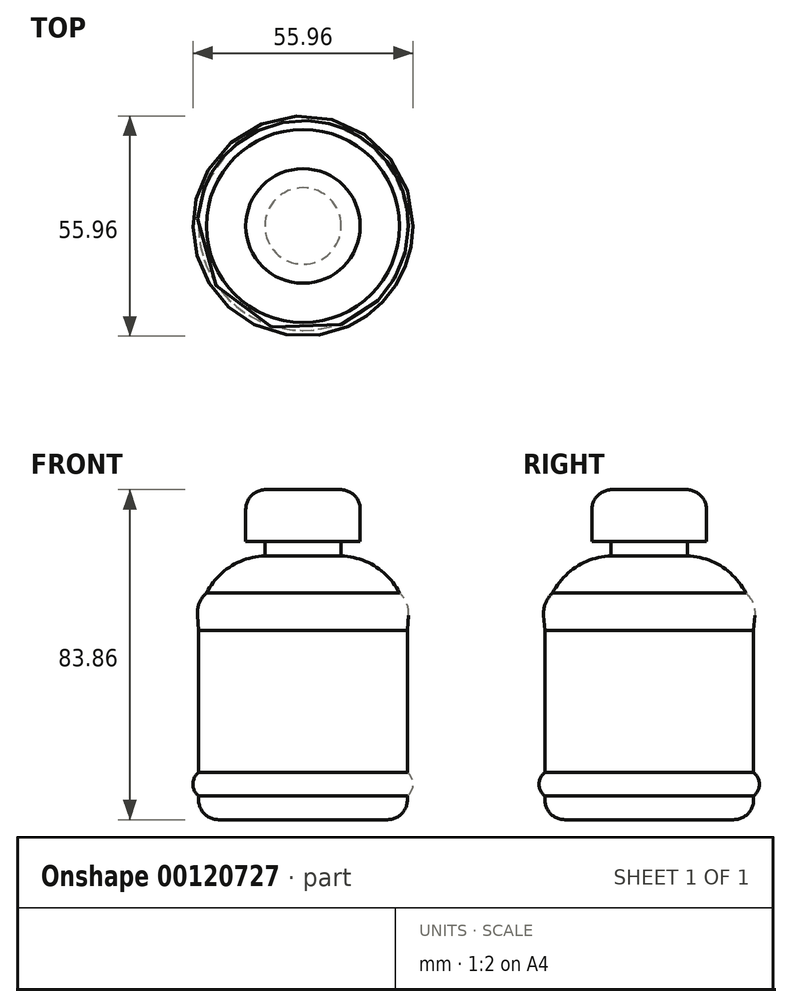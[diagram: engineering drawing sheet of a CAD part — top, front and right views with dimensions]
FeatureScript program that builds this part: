
annotation { "Feature Type Name" : "Feature", "Feature Type Description" : "" }
export const myFeature = defineFeature(function(context is Context, id is Id, definition is map)
    precondition{}
    {
        {
            var Q0;
            Q0=qCreatedBy(makeId("Front.planeOp"),FACE);
            var sketch = newSketch(context, id + "F0", { "sketchPlane" : qUnion([Q0])});
            skLineSegment(sketch, "E0", {"start": v(0, 52.34) * mm, "end": v(14.55, 52.34) * mm});
            skLineSegment(sketch, "E1", {"start": v(14.55, 52.34) * mm, "end": v(14.55, 39.22) * mm});
            skLineSegment(sketch, "E2", {"start": v(14.55, 39.22) * mm, "end": v(9.7, 39.22) * mm});
            skLineSegment(sketch, "E3", {"start": v(9.7, 39.22) * mm, "end": v(9.7, 35.51) * mm});
            skArc(sketch, "E4", {"start": v(24.53, 26.1) * mm, "mid": v(18.38, 32.8) * mm, "end": v(9.7, 35.51) * mm});
            skArc(sketch, "E5", {"start": v(26.81, 20.4) * mm, "mid": v(26.33, 23.51) * mm, "end": v(24.53, 26.1) * mm});
            skLineSegment(sketch, "E6", {"start": v(26.81, 20.4) * mm, "end": v(26.53, 16.6) * mm});
            skLineSegment(sketch, "E7", {"start": v(26.53, 16.6) * mm, "end": v(26.53, -19.54) * mm});
            skArc(sketch, "E8", {"start": v(26.53, -25.53) * mm, "mid": v(27.98, -22.53) * mm, "end": v(26.53, -19.54) * mm});
            skLineSegment(sketch, "E9", {"start": v(26.53, -25.53) * mm, "end": v(26.53, -31.52) * mm});
            skLineSegment(sketch, "E10", {"start": v(26.53, -31.52) * mm, "end": v(0, -31.52) * mm});
            skLineSegment(sketch, "E11", {"start": v(0, 52.34) * mm, "end": v(0, -31.52) * mm});
            skSolve(sketch);
        }
        {
            var Q0;
            Q0=makeQuery(id+"F0.imprint","IMPRINT",FACE,{"disambiguationData":[TD([[makeQuery(id+"F0.imprint","IMPRINT",EDGE,{"derivedFrom":sQuery(id+"F0.wireOp",EDGE,"E0")}),-1.0]])]});
            var Q1;
            Q1=sQuery(id+"F0.wireOp",EDGE,"E11");
            revolve(context, id + "F1", {"entities" : qUnion([Q0]), "axis" : qUnion([Q1]), "revolveType" : RevolveType.FULL});
        }
        {
            var Q0;
            Q0=makeQuery(id+"F1.opRevolve","SWEPT_EDGE",EDGE,{"disambiguationData":[OSD([sQuery(id+"F0.wireOp",EDGE,"E0"),sQuery(id+"F0.wireOp",EDGE,"E1")])]});
            var Q1;
            Q1=makeQuery(id+"F1.opRevolve","SWEPT_EDGE",EDGE,{"disambiguationData":[OSD([sQuery(id+"F0.wireOp",EDGE,"E9"),sQuery(id+"F0.wireOp",EDGE,"E10")])]});
            fillet(context, id + "F2", {"entities" : qUnion([Q0, Q1]), "radius" : 5.08 * mm, "tangentPropagation" : true, "allowEdgeOverflow" : false});
        }
        {
            var Q0;
            Q0=makeQuery(id+"F1.opRevolve","SWEPT_BODY",BODY,{"disambiguationData":[OSD([sQuery(id+"F0.wireOp",EDGE,"E0"),sQuery(id+"F0.wireOp",EDGE,"E1"),sQuery(id+"F0.wireOp",EDGE,"E2"),sQuery(id+"F0.wireOp",EDGE,"E3"),sQuery(id+"F0.wireOp",EDGE,"E4"),sQuery(id+"F0.wireOp",EDGE,"E5"),sQuery(id+"F0.wireOp",EDGE,"E6"),sQuery(id+"F0.wireOp",EDGE,"E7"),sQuery(id+"F0.wireOp",EDGE,"E8"),sQuery(id+"F0.wireOp",EDGE,"E9"),sQuery(id+"F0.wireOp",EDGE,"E10"),sQuery(id+"F0.wireOp",EDGE,"E11")])]});
            transform(context, id + "F3", {"entities" : qUnion([Q0]), "transformType" : TransformType.TRANSLATION_3D, "dx" : 0 * mm, "dy" : 0 * mm, "dz" : 0 * mm, "makeCopy" : true});
        }
    });
